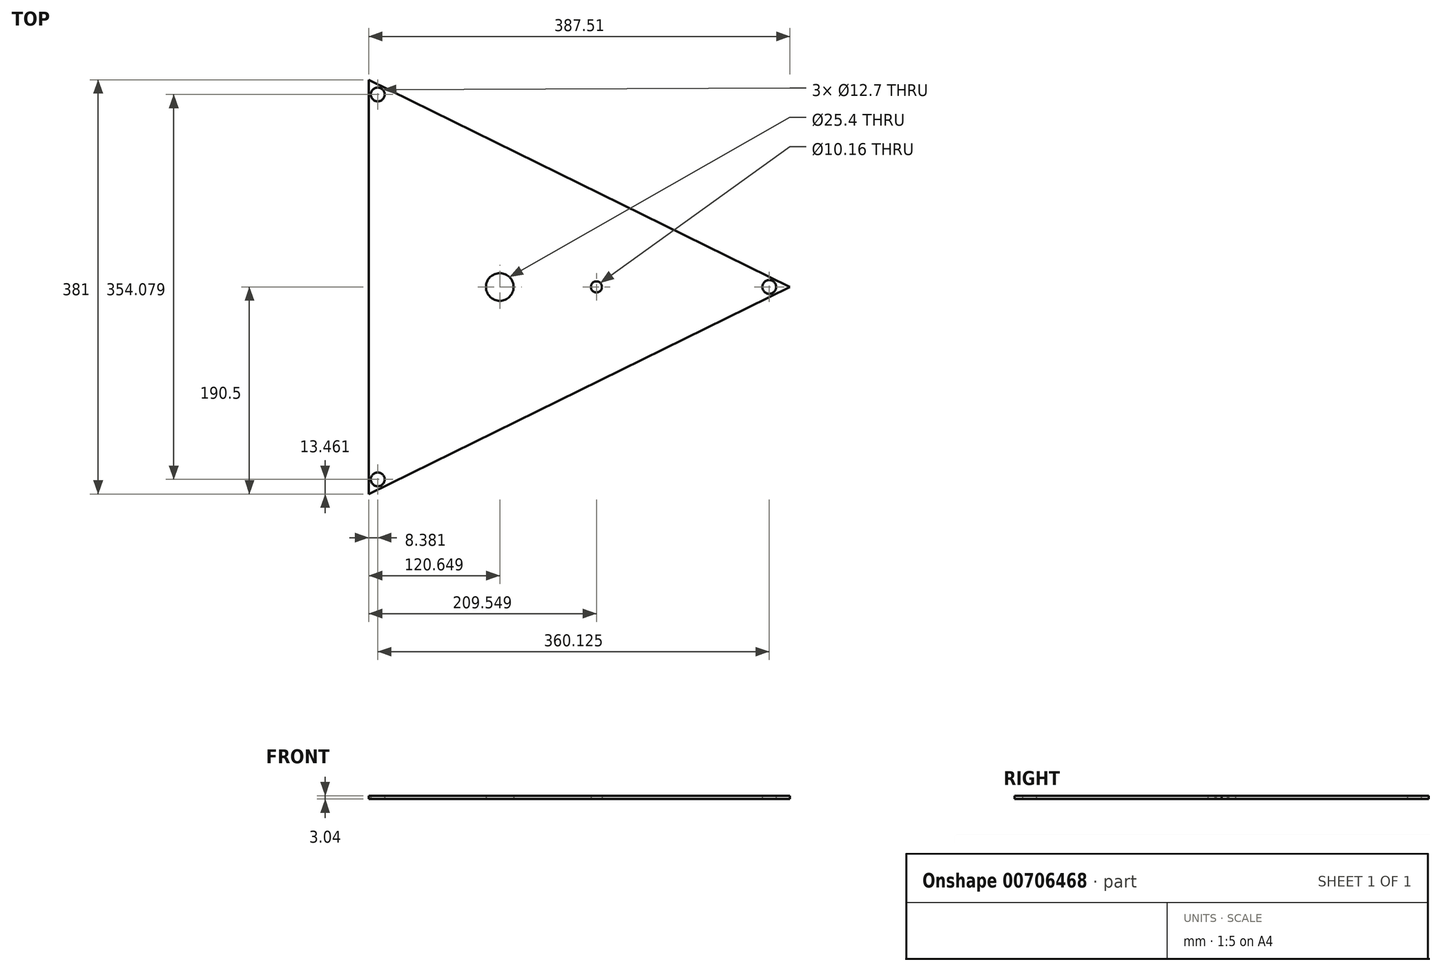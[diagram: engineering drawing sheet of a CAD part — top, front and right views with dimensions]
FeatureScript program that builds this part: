
annotation { "Feature Type Name" : "Feature", "Feature Type Description" : "" }
export const myFeature = defineFeature(function(context is Context, id is Id, definition is map)
    precondition{}
    {
        {
            var Q0;
            Q0=qCreatedBy(makeId("Top.planeOp"),FACE);
            var sketch = newSketch(context, id + "F0", { "sketchPlane" : qUnion([Q0])});
            skLineSegment(sketch, "E0.0", {"start": v(290.39, 0) * mm, "end": v(-97.12, -190.5) * mm});
            skLineSegment(sketch, "E0.1", {"start": v(-97.12, -190.5) * mm, "end": v(-97.12, 190.5) * mm});
            skLineSegment(sketch, "E0.2", {"start": v(-97.12, 190.5) * mm, "end": v(290.39, 0) * mm});
            skPoint(sketch, "E0.0.midPoint", {"position": v(76.2, 0) * mm});
            skCircle(sketch, "E1", {"center": v(88.83, 23.6) * mm, "radius": 2.48 * mm, "construction": true});
            skCircle(sketch, "E2", {"center": v(135.97, 23.6) * mm, "radius": 2.48 * mm, "construction": true});
            skCircle(sketch, "E3", {"center": v(88.83, -23.55) * mm, "radius": 2.48 * mm, "construction": true});
            skCircle(sketch, "E4", {"center": v(135.97, -23.55) * mm, "radius": 2.48 * mm, "construction": true});
            skCircle(sketch, "E5", {"center": v(112.43, 0) * mm, "radius": 5.08 * mm});
            skCircle(sketch, "E6", {"center": v(23.53, 0) * mm, "radius": 12.7 * mm});
            skCircle(sketch, "E7", {"center": v(23.53, 0) * mm, "radius": 9.53 * mm});
            skLineSegment(sketch, "E8.0", {"start": v(-95.09, 187.24) * mm, "end": v(285.78, 0) * mm, "construction": true});
            skLineSegment(sketch, "E8.1", {"start": v(-95.09, -187.24) * mm, "end": v(-95.09, 187.24) * mm, "construction": true});
            skLineSegment(sketch, "E8.2", {"start": v(285.78, 0) * mm, "end": v(-95.09, -187.24) * mm, "construction": true});
            skCircle(sketch, "E9", {"center": v(-88.74, -177.04) * mm, "radius": 6.35 * mm});
            skCircle(sketch, "E10", {"center": v(-88.74, 177.04) * mm, "radius": 6.35 * mm});
            skCircle(sketch, "E11", {"center": v(271.39, 0) * mm, "radius": 6.35 * mm});
            skCircle(sketch, "E12", {"center": v(-8.47, 32) * mm, "radius": 6 * mm, "construction": true});
            skCircle(sketch, "E13", {"center": v(55.53, 32) * mm, "radius": 6 * mm, "construction": true});
            skCircle(sketch, "E14", {"center": v(55.53, -32) * mm, "radius": 6 * mm, "construction": true});
            skCircle(sketch, "E15", {"center": v(-8.47, -32) * mm, "radius": 6 * mm, "construction": true});
            skLineSegment(sketch, "E16", {"start": v(290.39, 0) * mm, "end": v(-97.12, 0) * mm, "construction": true});
            skLineSegment(sketch, "E17", {"start": v(75.47, -105.65) * mm, "end": v(23.53, 0) * mm, "construction": true});
            skSolve(sketch);
        }
        {
            var Q0;
            Q0 = qSketchRegion(id + "F0", true);
            extrude(context, id + "F1", {"entities" : qUnion([Q0]), "depth" : 3.04 * mm, "offsetDistance" : 25.4 * mm});
        }
    });
